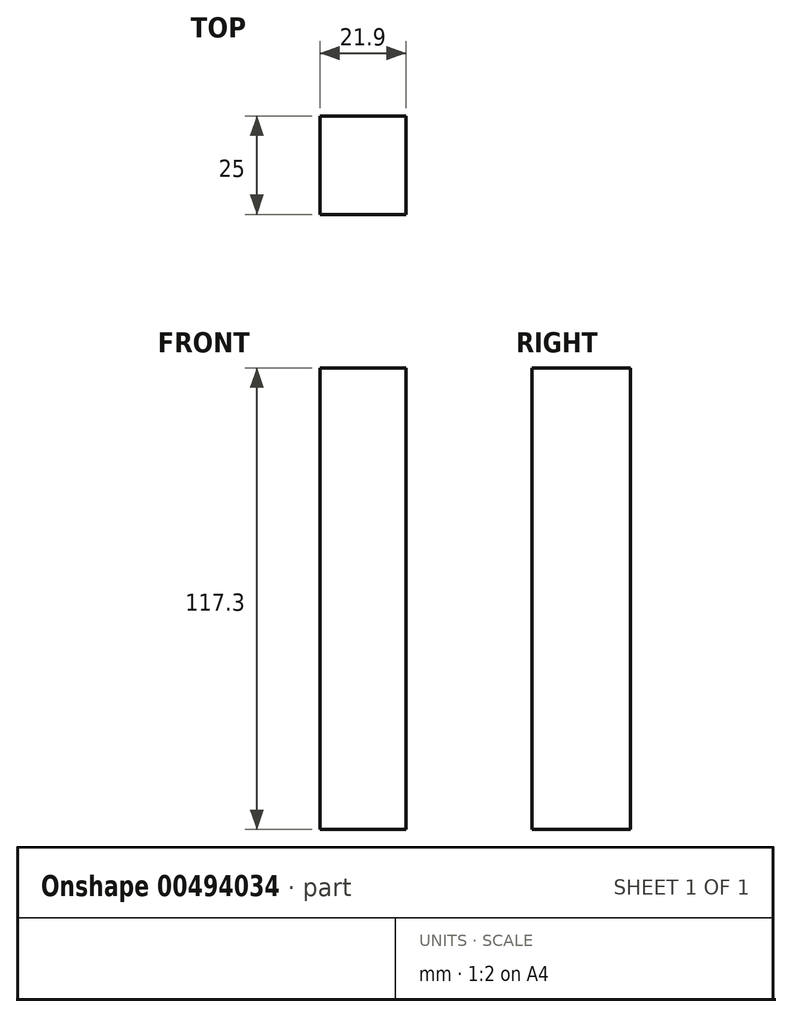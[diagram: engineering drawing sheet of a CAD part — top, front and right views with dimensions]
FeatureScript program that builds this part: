
annotation { "Feature Type Name" : "Feature", "Feature Type Description" : "" }
export const myFeature = defineFeature(function(context is Context, id is Id, definition is map)
    precondition{}
    {
        {
            var Q0;
            Q0=qCreatedBy(makeId("Front.planeOp"),FACE);
            var sketch = newSketch(context, id + "F0", { "sketchPlane" : qUnion([Q0])});
            skLineSegment(sketch, "E0.bottom", {"start": v(-10.95, -58.65) * mm, "end": v(10.95, -58.65) * mm});
            skLineSegment(sketch, "E0.top", {"start": v(-10.95, 58.65) * mm, "end": v(10.95, 58.65) * mm});
            skLineSegment(sketch, "E0.left", {"start": v(-10.95, -58.65) * mm, "end": v(-10.95, 58.65) * mm});
            skLineSegment(sketch, "E0.right", {"start": v(10.95, -58.65) * mm, "end": v(10.95, 58.65) * mm});
            skPoint(sketch, "E0.middle", {"position": v(0, 0) * mm});
            skSolve(sketch);
        }
        {
            var Q0;
            Q0=makeQuery(id+"F0.imprint","IMPRINT",FACE,{"disambiguationData":[TD([[makeQuery(id+"F0.imprint","IMPRINT",EDGE,{"derivedFrom":sQuery(id+"F0.wireOp",EDGE,"E0.bottom")}),1.0]])]});
            extrude(context, id + "F1", {"entities" : qUnion([Q0]), "depth" : 25 * mm});
        }
    });
